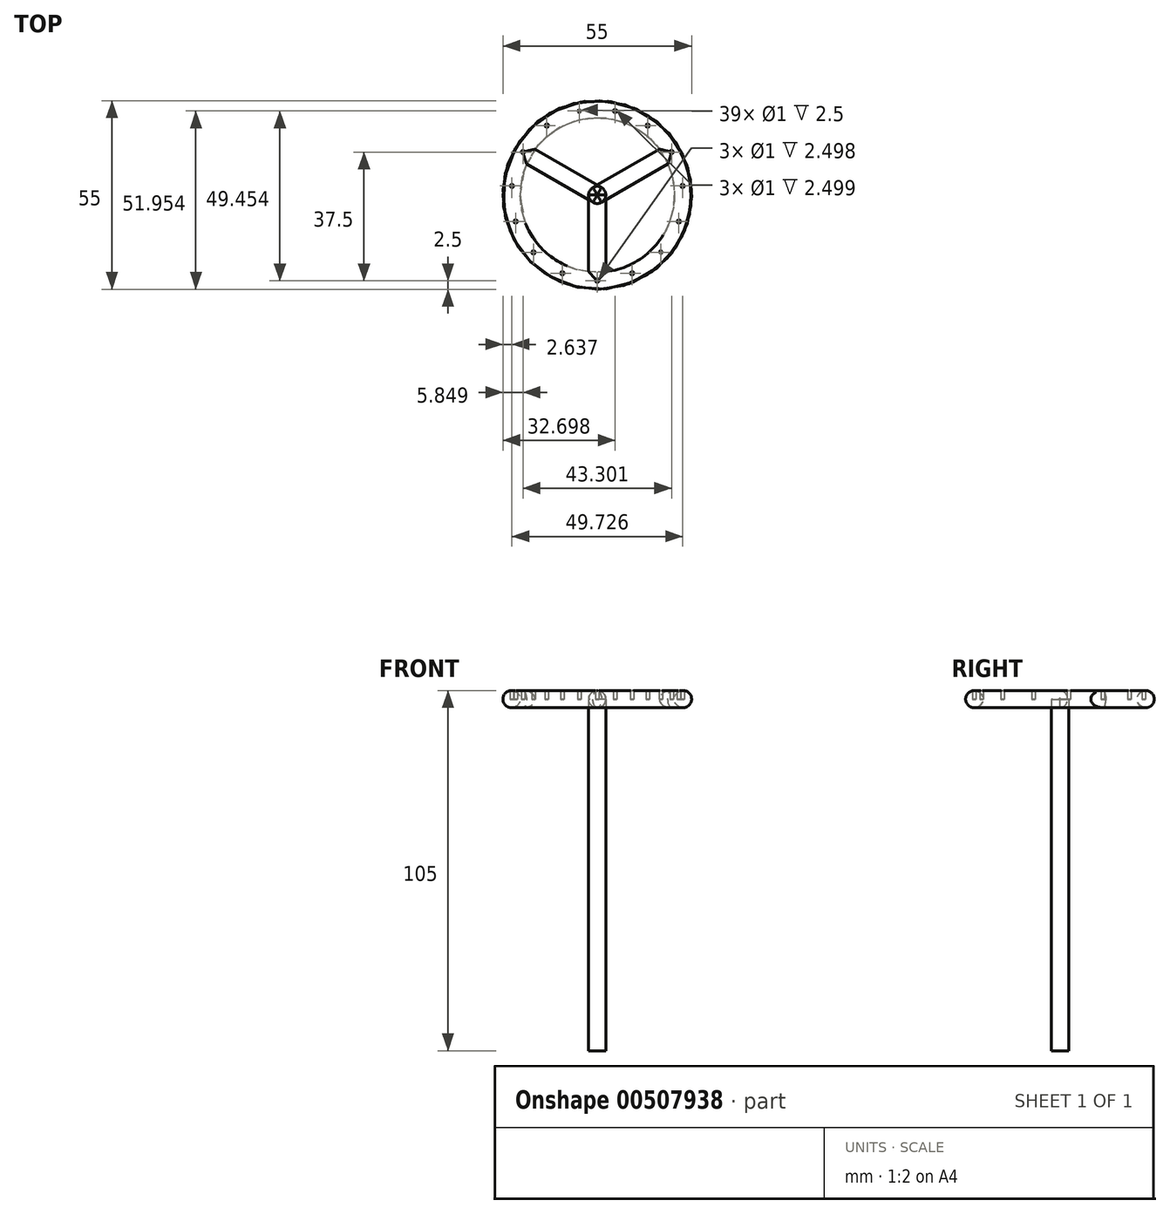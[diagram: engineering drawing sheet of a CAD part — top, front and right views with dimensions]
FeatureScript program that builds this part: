
annotation { "Feature Type Name" : "Feature", "Feature Type Description" : "" }
export const myFeature = defineFeature(function(context is Context, id is Id, definition is map)
    precondition{}
    {
        {
            var Q0;
            Q0=qCreatedBy(makeId("Top.planeOp"),FACE);
            var sketch = newSketch(context, id + "F0", { "sketchPlane" : qUnion([Q0])});
            skCircle(sketch, "E0", {"center": v(0, 0) * mm, "radius": 25 * mm});
            skLineSegment(sketch, "E1", {"start": v(0, 0) * mm, "end": v(-21.65, 12.5) * mm});
            skLineSegment(sketch, "E2", {"start": v(0, 0) * mm, "end": v(21.65, 12.5) * mm});
            skLineSegment(sketch, "E3", {"start": v(0, 0) * mm, "end": v(0, -25) * mm});
            skSolve(sketch);
        }
        {
            var Q0;
            Q0=qCreatedBy(makeId("Front.planeOp"),FACE);
            var sketch = newSketch(context, id + "F1", { "sketchPlane" : qUnion([Q0])});
            skLineSegment(sketch, "E4", {"start": v(0, 0) * mm, "end": v(0, -102.5) * mm});
            skSolve(sketch);
        }
        {
            var Q0;
            Q0=qCreatedBy(makeId("Front.planeOp"),FACE);
            var sketch = newSketch(context, id + "F2", { "sketchPlane" : qUnion([Q0])});
            skCircle(sketch, "E5", {"center": v(-25, 0) * mm, "radius": 2.5 * mm});
            skSolve(sketch);
        }
        {
            var Q0;
            Q0=makeQuery(id+"F2.imprint","IMPRINT",FACE,{"disambiguationData":[TD([[makeQuery(id+"F2.imprint","IMPRINT",EDGE,{"derivedFrom":sQuery(id+"F2.wireOp",EDGE,"E5")}),1.0]])]});
            var Q1;
            Q1=sQuery(id+"F0.wireOp",EDGE,"E0");
            sweep(context, id + "F3", {"profiles" : qUnion([Q0]), "path" : qUnion([Q1])});
        }
        {
            var Q0;
            Q0=qCreatedBy(makeId("Front.planeOp"),FACE);
            var sketch = newSketch(context, id + "F4", { "sketchPlane" : qUnion([Q0])});
            skCircle(sketch, "E6", {"center": v(0, 0) * mm, "radius": 2.5 * mm});
            skSolve(sketch);
        }
        {
            var Q0;
            Q0=makeQuery(id+"F4.imprint","IMPRINT",FACE,{"disambiguationData":[TD([[makeQuery(id+"F4.imprint","IMPRINT",EDGE,{"derivedFrom":sQuery(id+"F4.wireOp",EDGE,"E6")}),1.0]])]});
            var Q1;
            Q1=sQuery(id+"F0.wireOp",EDGE,"E3");
            sweep(context, id + "F5", {"operationType" : NewBodyOperationType.ADD, "profiles" : qUnion([Q0]), "path" : qUnion([Q1])});
        }
        {
            var Q0;
            Q0=makeQuery(id+"F3.opSweep","SWEPT_BODY",BODY,{"disambiguationData":[OSD([sQuery(id+"F0.wireOp",EDGE,"E0"),sQuery(id+"F2.wireOp",EDGE,"E5")])]});
            var Q1;
            Q1=sQuery(id+"F1.wireOp",EDGE,"E4");
            circularPattern(context, id + "F6", {"entities" : qUnion([Q0]), "axis" : qUnion([Q1]), "angle" : 360 * degree, "instanceCount" : 3, "equalSpace" : true});
        }
        {
            var Q0;
            Q0=qCreatedBy(makeId("Top.planeOp"),FACE);
            var sketch = newSketch(context, id + "F7", { "sketchPlane" : qUnion([Q0])});
            skCircle(sketch, "E7", {"center": v(0, 0) * mm, "radius": 2.5 * mm});
            skSolve(sketch);
        }
        {
            var Q0;
            Q0=qSketchRegion(id+"F7",true);
            var Q1;
            Q1=sQuery(id+"F1.wireOp",EDGE,"E4");
            sweep(context, id + "F8", {"profiles" : qUnion([Q0]), "path" : qUnion([Q1])});
        }
        {
            var Q0;
            Q0=qCreatedBy(makeId("Top.planeOp"),FACE);
            var sketch = newSketch(context, id + "F9", { "sketchPlane" : qUnion([Q0])});
            skCircle(sketch, "E8", {"center": v(0, -25) * mm, "radius": 0.5 * mm});
            skSolve(sketch);
        }
        {
            var Q0;
            Q0=qSketchRegion(id+"F9",true);
            extrude(context, id + "F10", {"entities" : qUnion([Q0]), "depth" : 2.5 * mm});
        }
        {
            var Q0;
            Q0=makeQuery(id+"F10.opExtrude","SWEPT_BODY",BODY,{"disambiguationData":[OSD([sQuery(id+"F9.wireOp",EDGE,"E8")])]});
            var Q1;
            Q1=sQuery(id+"F1.wireOp",EDGE,"E4");
            circularPattern(context, id + "F11", {"entities" : qUnion([Q0]), "axis" : qUnion([Q1]), "angle" : 360 * degree, "instanceCount" : 15, "equalSpace" : true});
        }
        {
            var Q0;
            Q0=makeQuery(id+"F11.opPattern","COPY",BODY,{"derivedFrom":makeQuery(id+"F10.opExtrude","SWEPT_BODY",BODY,{"disambiguationData":[OSD([sQuery(id+"F9.wireOp",EDGE,"E8")])]}),"instanceName":"1"});
            var Q1;
            Q1=makeQuery(id+"F11.opPattern","COPY",BODY,{"derivedFrom":makeQuery(id+"F10.opExtrude","SWEPT_BODY",BODY,{"disambiguationData":[OSD([sQuery(id+"F9.wireOp",EDGE,"E8")])]}),"instanceName":"23"});
            var Q2;
            Q2=makeQuery(id+"F11.opPattern","COPY",BODY,{"derivedFrom":makeQuery(id+"F10.opExtrude","SWEPT_BODY",BODY,{"disambiguationData":[OSD([sQuery(id+"F9.wireOp",EDGE,"E8")])]}),"instanceName":"22"});
            var Q3;
            Q3=makeQuery(id+"F11.opPattern","COPY",BODY,{"derivedFrom":makeQuery(id+"F10.opExtrude","SWEPT_BODY",BODY,{"disambiguationData":[OSD([sQuery(id+"F9.wireOp",EDGE,"E8")])]}),"instanceName":"21"});
            var Q4;
            Q4=makeQuery(id+"F11.opPattern","COPY",BODY,{"derivedFrom":makeQuery(id+"F10.opExtrude","SWEPT_BODY",BODY,{"disambiguationData":[OSD([sQuery(id+"F9.wireOp",EDGE,"E8")])]}),"instanceName":"20"});
            var Q5;
            Q5=makeQuery(id+"F11.opPattern","COPY",BODY,{"derivedFrom":makeQuery(id+"F10.opExtrude","SWEPT_BODY",BODY,{"disambiguationData":[OSD([sQuery(id+"F9.wireOp",EDGE,"E8")])]}),"instanceName":"19"});
            var Q6;
            Q6=makeQuery(id+"F11.opPattern","COPY",BODY,{"derivedFrom":makeQuery(id+"F10.opExtrude","SWEPT_BODY",BODY,{"disambiguationData":[OSD([sQuery(id+"F9.wireOp",EDGE,"E8")])]}),"instanceName":"18"});
            var Q7;
            Q7=makeQuery(id+"F11.opPattern","COPY",BODY,{"derivedFrom":makeQuery(id+"F10.opExtrude","SWEPT_BODY",BODY,{"disambiguationData":[OSD([sQuery(id+"F9.wireOp",EDGE,"E8")])]}),"instanceName":"17"});
            var Q8;
            Q8=makeQuery(id+"F11.opPattern","COPY",BODY,{"derivedFrom":makeQuery(id+"F10.opExtrude","SWEPT_BODY",BODY,{"disambiguationData":[OSD([sQuery(id+"F9.wireOp",EDGE,"E8")])]}),"instanceName":"16"});
            var Q9;
            Q9=makeQuery(id+"F11.opPattern","COPY",BODY,{"derivedFrom":makeQuery(id+"F10.opExtrude","SWEPT_BODY",BODY,{"disambiguationData":[OSD([sQuery(id+"F9.wireOp",EDGE,"E8")])]}),"instanceName":"15"});
            var Q10;
            Q10=makeQuery(id+"F11.opPattern","COPY",BODY,{"derivedFrom":makeQuery(id+"F10.opExtrude","SWEPT_BODY",BODY,{"disambiguationData":[OSD([sQuery(id+"F9.wireOp",EDGE,"E8")])]}),"instanceName":"14"});
            var Q11;
            Q11=makeQuery(id+"F11.opPattern","COPY",BODY,{"derivedFrom":makeQuery(id+"F10.opExtrude","SWEPT_BODY",BODY,{"disambiguationData":[OSD([sQuery(id+"F9.wireOp",EDGE,"E8")])]}),"instanceName":"13"});
            var Q12;
            Q12=makeQuery(id+"F11.opPattern","COPY",BODY,{"derivedFrom":makeQuery(id+"F10.opExtrude","SWEPT_BODY",BODY,{"disambiguationData":[OSD([sQuery(id+"F9.wireOp",EDGE,"E8")])]}),"instanceName":"12"});
            var Q13;
            Q13=makeQuery(id+"F11.opPattern","COPY",BODY,{"derivedFrom":makeQuery(id+"F10.opExtrude","SWEPT_BODY",BODY,{"disambiguationData":[OSD([sQuery(id+"F9.wireOp",EDGE,"E8")])]}),"instanceName":"11"});
            var Q14;
            Q14=makeQuery(id+"F11.opPattern","COPY",BODY,{"derivedFrom":makeQuery(id+"F10.opExtrude","SWEPT_BODY",BODY,{"disambiguationData":[OSD([sQuery(id+"F9.wireOp",EDGE,"E8")])]}),"instanceName":"10"});
            var Q15;
            Q15=makeQuery(id+"F11.opPattern","COPY",BODY,{"derivedFrom":makeQuery(id+"F10.opExtrude","SWEPT_BODY",BODY,{"disambiguationData":[OSD([sQuery(id+"F9.wireOp",EDGE,"E8")])]}),"instanceName":"9"});
            var Q16;
            Q16=makeQuery(id+"F11.opPattern","COPY",BODY,{"derivedFrom":makeQuery(id+"F10.opExtrude","SWEPT_BODY",BODY,{"disambiguationData":[OSD([sQuery(id+"F9.wireOp",EDGE,"E8")])]}),"instanceName":"8"});
            var Q17;
            Q17=makeQuery(id+"F11.opPattern","COPY",BODY,{"derivedFrom":makeQuery(id+"F10.opExtrude","SWEPT_BODY",BODY,{"disambiguationData":[OSD([sQuery(id+"F9.wireOp",EDGE,"E8")])]}),"instanceName":"7"});
            var Q18;
            Q18=makeQuery(id+"F11.opPattern","COPY",BODY,{"derivedFrom":makeQuery(id+"F10.opExtrude","SWEPT_BODY",BODY,{"disambiguationData":[OSD([sQuery(id+"F9.wireOp",EDGE,"E8")])]}),"instanceName":"6"});
            var Q19;
            Q19=makeQuery(id+"F11.opPattern","COPY",BODY,{"derivedFrom":makeQuery(id+"F10.opExtrude","SWEPT_BODY",BODY,{"disambiguationData":[OSD([sQuery(id+"F9.wireOp",EDGE,"E8")])]}),"instanceName":"5"});
            var Q20;
            Q20=makeQuery(id+"F11.opPattern","COPY",BODY,{"derivedFrom":makeQuery(id+"F10.opExtrude","SWEPT_BODY",BODY,{"disambiguationData":[OSD([sQuery(id+"F9.wireOp",EDGE,"E8")])]}),"instanceName":"4"});
            var Q21;
            Q21=makeQuery(id+"F11.opPattern","COPY",BODY,{"derivedFrom":makeQuery(id+"F10.opExtrude","SWEPT_BODY",BODY,{"disambiguationData":[OSD([sQuery(id+"F9.wireOp",EDGE,"E8")])]}),"instanceName":"3"});
            var Q22;
            Q22=makeQuery(id+"F11.opPattern","COPY",BODY,{"derivedFrom":makeQuery(id+"F10.opExtrude","SWEPT_BODY",BODY,{"disambiguationData":[OSD([sQuery(id+"F9.wireOp",EDGE,"E8")])]}),"instanceName":"2"});
            var Q23;
            Q23=makeQuery(id+"FsdLYlgyIIPtPH4_3.opPattern","COPY",BODY,{"derivedFrom":makeQuery(id+"F10.opExtrude","SWEPT_BODY",BODY,{"disambiguationData":[OSD([sQuery(id+"F9.wireOp",EDGE,"E8")])]}),"instanceName":"1"});
            var Q24;
            Q24=makeQuery(id+"FsdLYlgyIIPtPH4_3.opPattern","COPY",BODY,{"derivedFrom":makeQuery(id+"F10.opExtrude","SWEPT_BODY",BODY,{"disambiguationData":[OSD([sQuery(id+"F9.wireOp",EDGE,"E8")])]}),"instanceName":"2"});
            var Q25;
            Q25=makeQuery(id+"F10.opExtrude","SWEPT_BODY",BODY,{"disambiguationData":[OSD([sQuery(id+"F9.wireOp",EDGE,"E8")])]});
            var Q26;
            Q26=makeQuery(id+"FsdLYlgyIIPtPH4_3.opPattern","COPY",BODY,{"derivedFrom":makeQuery(id+"F10.opExtrude","SWEPT_BODY",BODY,{"disambiguationData":[OSD([sQuery(id+"F9.wireOp",EDGE,"E8")])]}),"instanceName":"3"});
            var Q27;
            Q27=makeQuery(id+"FsdLYlgyIIPtPH4_3.opPattern","COPY",BODY,{"derivedFrom":makeQuery(id+"F10.opExtrude","SWEPT_BODY",BODY,{"disambiguationData":[OSD([sQuery(id+"F9.wireOp",EDGE,"E8")])]}),"instanceName":"4"});
            var Q28;
            Q28=makeQuery(id+"F6GWW6hKw0zD2fU_3.opPattern","COPY",BODY,{"derivedFrom":makeQuery(id+"FsdLYlgyIIPtPH4_3.opPattern","COPY",BODY,{"derivedFrom":makeQuery(id+"F10.opExtrude","SWEPT_BODY",BODY,{"disambiguationData":[OSD([sQuery(id+"F9.wireOp",EDGE,"E8")])]}),"instanceName":"4"}),"instanceName":"1"});
            var Q29;
            Q29=makeQuery(id+"F6GWW6hKw0zD2fU_3.opPattern","COPY",BODY,{"derivedFrom":makeQuery(id+"FsdLYlgyIIPtPH4_3.opPattern","COPY",BODY,{"derivedFrom":makeQuery(id+"F10.opExtrude","SWEPT_BODY",BODY,{"disambiguationData":[OSD([sQuery(id+"F9.wireOp",EDGE,"E8")])]}),"instanceName":"3"}),"instanceName":"1"});
            var Q30;
            Q30=makeQuery(id+"F6GWW6hKw0zD2fU_3.opPattern","COPY",BODY,{"derivedFrom":makeQuery(id+"FsdLYlgyIIPtPH4_3.opPattern","COPY",BODY,{"derivedFrom":makeQuery(id+"F10.opExtrude","SWEPT_BODY",BODY,{"disambiguationData":[OSD([sQuery(id+"F9.wireOp",EDGE,"E8")])]}),"instanceName":"2"}),"instanceName":"1"});
            var Q31;
            Q31=makeQuery(id+"F6GWW6hKw0zD2fU_3.opPattern","COPY",BODY,{"derivedFrom":makeQuery(id+"FsdLYlgyIIPtPH4_3.opPattern","COPY",BODY,{"derivedFrom":makeQuery(id+"F10.opExtrude","SWEPT_BODY",BODY,{"disambiguationData":[OSD([sQuery(id+"F9.wireOp",EDGE,"E8")])]}),"instanceName":"1"}),"instanceName":"1"});
            var Q32;
            Q32=makeQuery(id+"F6GWW6hKw0zD2fU_3.opPattern","COPY",BODY,{"derivedFrom":makeQuery(id+"FsdLYlgyIIPtPH4_3.opPattern","COPY",BODY,{"derivedFrom":makeQuery(id+"F10.opExtrude","SWEPT_BODY",BODY,{"disambiguationData":[OSD([sQuery(id+"F9.wireOp",EDGE,"E8")])]}),"instanceName":"4"}),"instanceName":"2"});
            var Q33;
            Q33=makeQuery(id+"FsdLYlgyIIPtPH4_3.opPattern","COPY",BODY,{"derivedFrom":makeQuery(id+"F10.opExtrude","SWEPT_BODY",BODY,{"disambiguationData":[OSD([sQuery(id+"F9.wireOp",EDGE,"E8")])]}),"instanceName":"5"});
            var Q34;
            Q34=makeQuery(id+"F6GWW6hKw0zD2fU_3.opPattern","COPY",BODY,{"derivedFrom":makeQuery(id+"FsdLYlgyIIPtPH4_3.opPattern","COPY",BODY,{"derivedFrom":makeQuery(id+"F10.opExtrude","SWEPT_BODY",BODY,{"disambiguationData":[OSD([sQuery(id+"F9.wireOp",EDGE,"E8")])]}),"instanceName":"3"}),"instanceName":"2"});
            var Q35;
            Q35=makeQuery(id+"F6GWW6hKw0zD2fU_3.opPattern","COPY",BODY,{"derivedFrom":makeQuery(id+"FsdLYlgyIIPtPH4_3.opPattern","COPY",BODY,{"derivedFrom":makeQuery(id+"F10.opExtrude","SWEPT_BODY",BODY,{"disambiguationData":[OSD([sQuery(id+"F9.wireOp",EDGE,"E8")])]}),"instanceName":"2"}),"instanceName":"2"});
            var Q36;
            Q36=makeQuery(id+"F6GWW6hKw0zD2fU_3.opPattern","COPY",BODY,{"derivedFrom":makeQuery(id+"FsdLYlgyIIPtPH4_3.opPattern","COPY",BODY,{"derivedFrom":makeQuery(id+"F10.opExtrude","SWEPT_BODY",BODY,{"disambiguationData":[OSD([sQuery(id+"F9.wireOp",EDGE,"E8")])]}),"instanceName":"1"}),"instanceName":"2"});
            var Q37;
            Q37=makeQuery(id+"F6GWW6hKw0zD2fU_3.opPattern","COPY",BODY,{"derivedFrom":makeQuery(id+"FsdLYlgyIIPtPH4_3.opPattern","COPY",BODY,{"derivedFrom":makeQuery(id+"F10.opExtrude","SWEPT_BODY",BODY,{"disambiguationData":[OSD([sQuery(id+"F9.wireOp",EDGE,"E8")])]}),"instanceName":"5"}),"instanceName":"1"});
            var Q38;
            Q38=makeQuery(id+"F3.opSweep","SWEPT_BODY",BODY,{"disambiguationData":[OSD([sQuery(id+"F0.wireOp",EDGE,"E0"),sQuery(id+"F2.wireOp",EDGE,"E5")])]});
            var Q39;
            Q39=makeQuery(id+"F6.opPattern","COPY",BODY,{"derivedFrom":makeQuery(id+"F3.opSweep","SWEPT_BODY",BODY,{"disambiguationData":[OSD([sQuery(id+"F0.wireOp",EDGE,"E0"),sQuery(id+"F2.wireOp",EDGE,"E5")])]}),"instanceName":"1"});
            var Q40;
            Q40=makeQuery(id+"F8.opSweep","SWEPT_BODY",BODY,{"disambiguationData":[OSD([sQuery(id+"F1.wireOp",EDGE,"E4"),sQuery(id+"F7.wireOp",EDGE,"E7")])]});
            var Q41;
            Q41=makeQuery(id+"F6.opPattern","COPY",BODY,{"derivedFrom":makeQuery(id+"F3.opSweep","SWEPT_BODY",BODY,{"disambiguationData":[OSD([sQuery(id+"F0.wireOp",EDGE,"E0"),sQuery(id+"F2.wireOp",EDGE,"E5")])]}),"instanceName":"2"});
            booleanBodies(context, id + "F12", {"operationType" : BooleanOperationType.SUBTRACTION, "tools" : qUnion([Q0, Q1, Q2, Q3, Q4, Q5, Q6, Q7, Q8, Q9, Q10, Q11, Q12, Q13, Q14, Q15, Q16, Q17, Q18, Q19, Q20, Q21, Q22, Q23, Q24, Q25, Q26, Q27, Q28, Q29, Q30, Q31, Q32, Q33, Q34, Q35, Q36, Q37]), "targets" : qUnion([Q38, Q39, Q40, Q41])});
        }
    });
